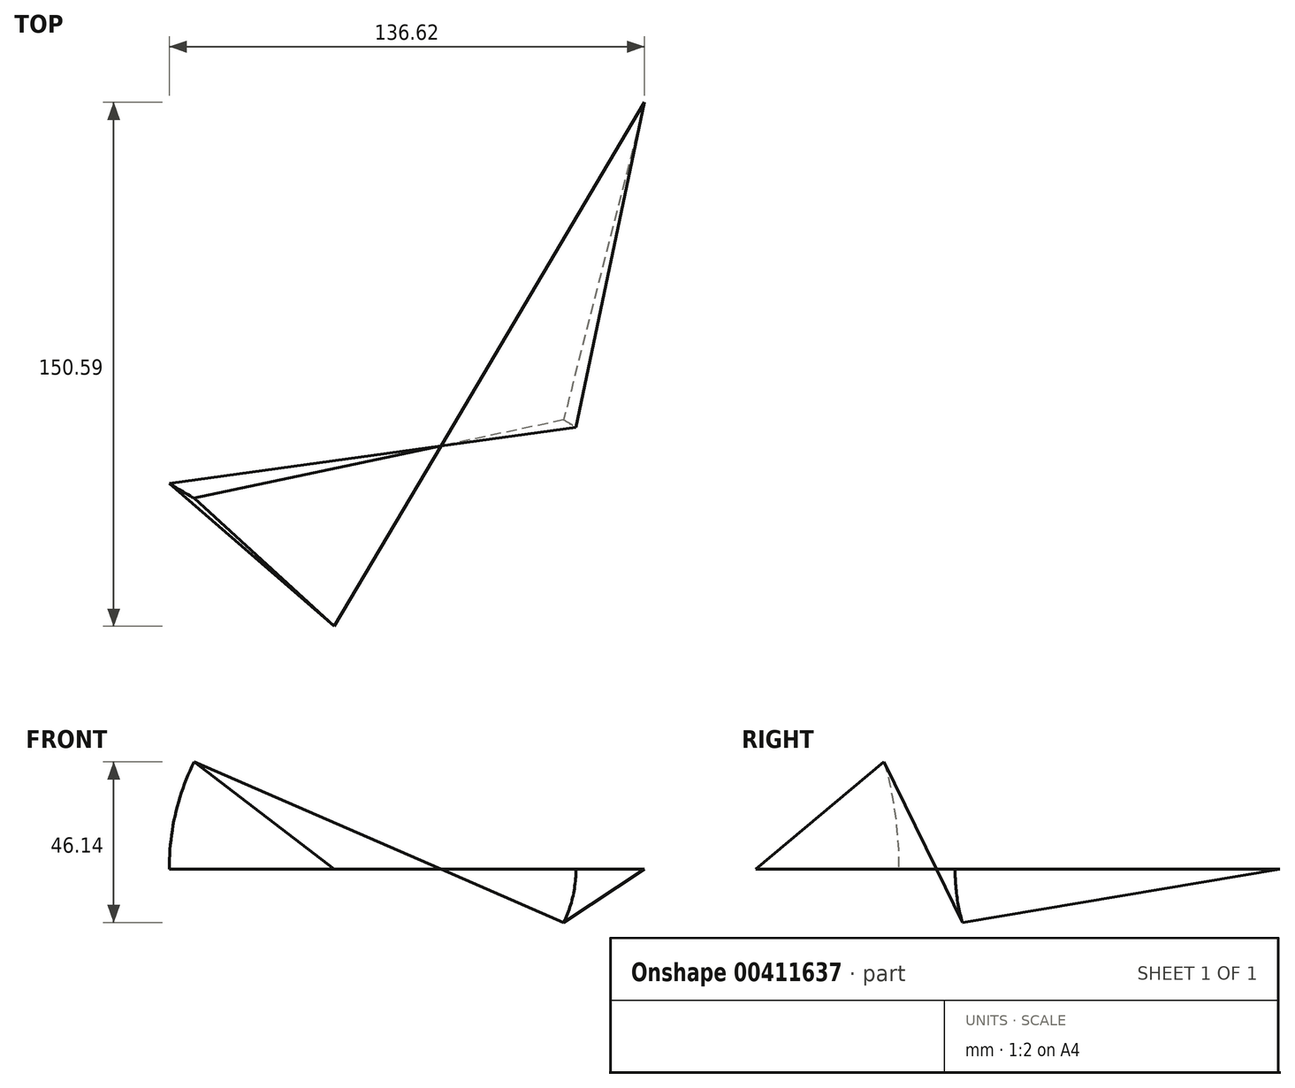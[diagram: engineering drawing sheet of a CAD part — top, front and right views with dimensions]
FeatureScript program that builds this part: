
annotation { "Feature Type Name" : "Feature", "Feature Type Description" : "" }
export const myFeature = defineFeature(function(context is Context, id is Id, definition is map)
    precondition{}
    {
        {
            var Q0;
            Q0=qCreatedBy(makeId("Top.planeOp"),FACE);
            var sketch = newSketch(context, id + "F0", { "sketchPlane" : qUnion([Q0])});
            skLineSegment(sketch, "E0", {"start": v(0, 0) * mm, "end": v(-116.88, -16.2) * mm});
            skLineSegment(sketch, "E1", {"start": v(-116.88, -16.2) * mm, "end": v(-69.52, -57.23) * mm});
            skLineSegment(sketch, "E2", {"start": v(-69.52, -57.23) * mm, "end": v(19.74, 93.36) * mm});
            skLineSegment(sketch, "E3", {"start": v(19.74, 93.36) * mm, "end": v(0, 0) * mm});
            skSolve(sketch);
        }
        {
            var Q0;
            Q0 = qSketchRegion(id + "F0", true);
            var Q1;
            Q1=sQuery(id+"F0.wireOp",EDGE,"E2");
            revolve(context, id + "F1", {"entities" : qUnion([Q0]), "axis" : qUnion([Q1]), "revolveType" : RevolveType.ONE_DIRECTION, "angle" : 30 * degree});
        }
    });
